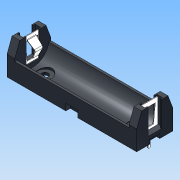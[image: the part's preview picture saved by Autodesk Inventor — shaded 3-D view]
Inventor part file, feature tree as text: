
AUTODESK INVENTOR PART (.ipt)
format: ipt  version: 2011 (Build 150239000, 239)  size: 469,504 bytes
history: native  units: mm
features: sketch x19, extrude x16, mirror x4, other x3, fillet x3, hole x1, sweep x1
ambient origin geometry x8: Origin, YZ Plane, XZ Plane, XY Plane, X Axis, Y Axis, Z Axis, Center Point
feature tree (47):
  other  "Твердое тело1"
  extrude  "Выдавливание1"  Depth=52.0mm
  extrude  "Выдавливание2"  Depth=26.0mm
  extrude  "Выдавливание3"  Depth=16.5mm
  extrude  "Выдавливание4"  Depth=8.25mm
  extrude  "Выдавливание5"  Depth=7.8mm TaperAngle=0.0deg
  extrude  "Выдавливание6"  Depth=14.637281mm
  extrude  "Выдавливание7"  Depth=1.0mm
  other  "РабПлоскость2"
  hole  "Отверстие1"  [1 undecoded]
  extrude  "Выдавливание8"  Depth=15.0mm
  extrude  "Выдавливание9"  Depth=2.25mm
  mirror  "Зеркальное отражение2"
  extrude  "Выдавливание10"  Depth=2.25mm
  extrude  "Выдавливание11"  Depth=1.2mm
  sketch  "Эскиз15"
  other  "РабПлоскость3"
  sweep  "Сдвиг1"
  extrude  "Выдавливание12"  Depth=3.5mm TaperAngle=0.0deg
  fillet  "Сопряжение1"  Radius=3.5mm
  fillet  "Сопряжение2"  Radius=6.0mm
  mirror  "Зеркальное отражение3"
  extrude  "Выдавливание13"  Depth=3.0mm
  sketch  "Эскиз20"
  extrude  "Выдавливание15"  Depth=3.5mm TaperAngle=0.0deg
  extrude  "Выдавливание16"  Depth=2.5mm
  fillet  "Сопряжение3"  Radius=0.5mm
  mirror  "Зеркальное отражение4"
  extrude  "Выдавливание17"  Depth=8.0mm
  mirror  "Зеркальное отражение5"
  sketch  "Эскиз1"
  sketch  "Эскиз2"
  sketch  "Эскиз3"
  sketch  "Эскиз4"
  sketch  "Эскиз5"
  sketch  "Эскиз6"
  sketch  "Эскиз7"
  sketch  "Эскиз10"
  sketch  "Эскиз11"
  sketch  "Эскиз12"
  sketch  "Эскиз13"
  sketch  "Эскиз14"
  sketch  "Эскиз17"
  sketch  "Эскиз18"
  sketch  "Эскиз19"
  sketch  "Эскиз22"
  sketch  "Эскиз23"
note: 1 required parameter value undecoded (feature->parameter linkage not recoverable at this tier; creation-order binding heuristic only, values carry confidence <= 0.55)
